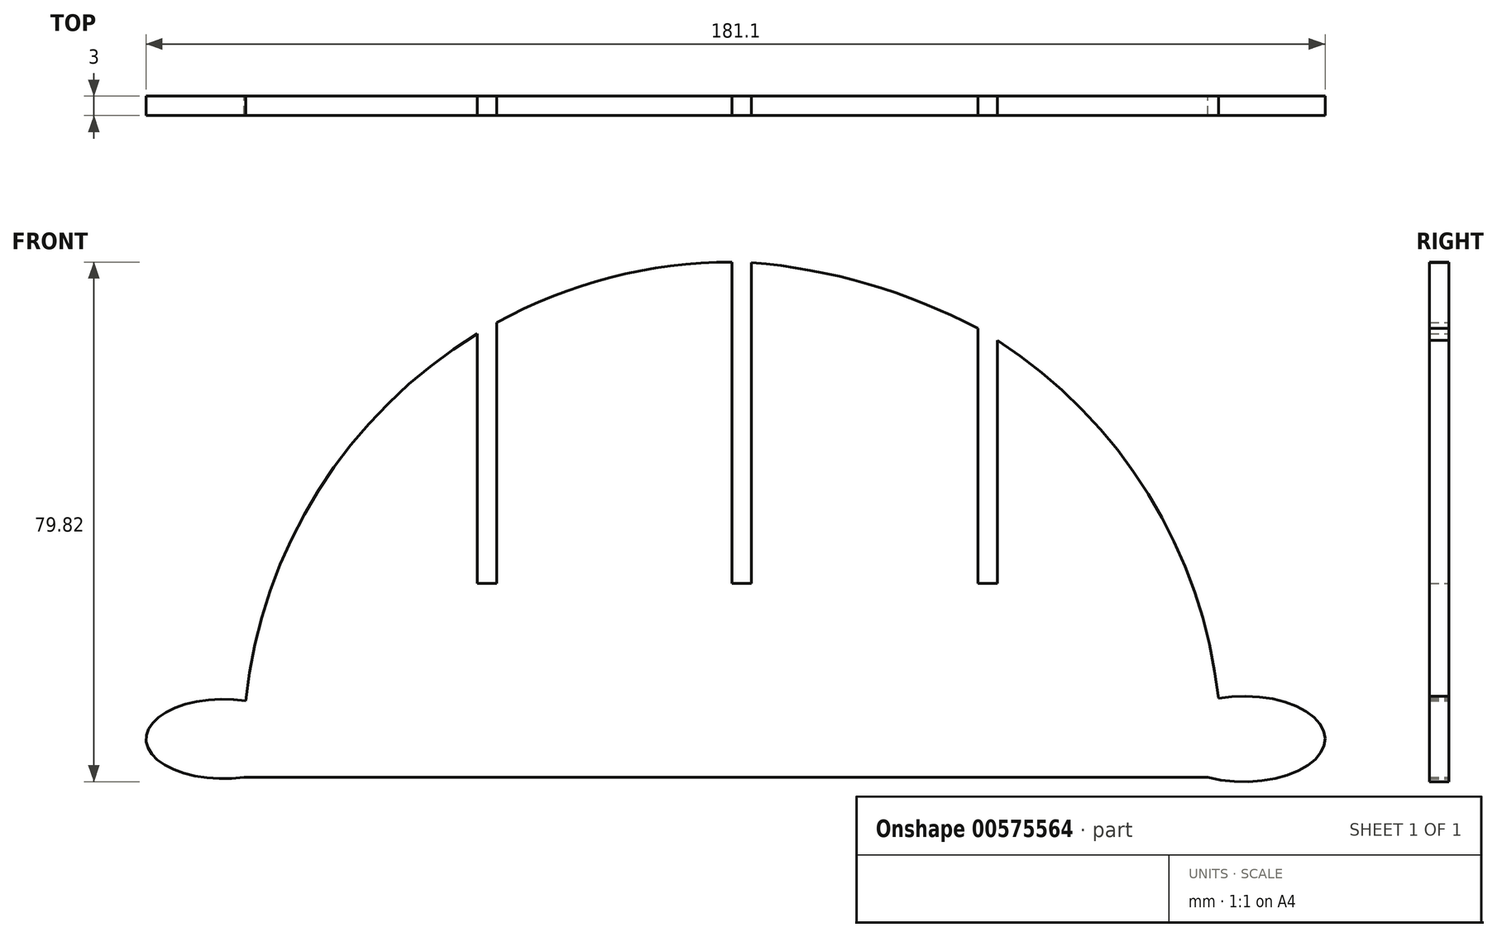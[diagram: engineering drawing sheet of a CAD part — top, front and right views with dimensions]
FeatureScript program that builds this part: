
annotation { "Feature Type Name" : "Feature", "Feature Type Description" : "" }
export const myFeature = defineFeature(function(context is Context, id is Id, definition is map)
    precondition{}
    {
        {
            var Q0;
            Q0=qCreatedBy(makeId("Front.planeOp"),FACE);
            var sketch = newSketch(context, id + "F0", { "sketchPlane" : qUnion([Q0])});
            skLineSegment(sketch, "E0", {"start": v(70.95, 0) * mm, "end": v(-79.05, 0) * mm});
            skArc(sketch, "E1.trimOffspring", {"start": v(70.65, 11.7) * mm, "mid": v(70.63, 11.92) * mm, "end": v(70.6, 12.13) * mm});
            skLineSegment(sketch, "E2", {"start": v(36.67, 29.76) * mm, "end": v(33.67, 29.76) * mm});
            skPoint(sketch, "E3.end.orphan", {"position": v(43.59, 29.76) * mm});
            skPoint(sketch, "E4.start.orphan", {"position": v(33.67, 68.95) * mm});
            skLineSegment(sketch, "E5", {"start": v(-1.1, 29.76) * mm, "end": v(-4.1, 29.76) * mm});
            skLineSegment(sketch, "E6", {"start": v(-40.23, 29.76) * mm, "end": v(-43.23, 29.76) * mm});
            skPoint(sketch, "E7.orphan", {"position": v(66.5, 29.76) * mm});
            skEllipticalArc(sketch, "E8", {});
            skPoint(sketch, "E9.orphan", {"position": v(-80.82, 0) * mm});
            skEllipticalArc(sketch, "E10", {});
            skArc(sketch, "E11.trimOffspring", {"start": v(70.62, 12.14) * mm, "mid": v(59.87, 43.47) * mm, "end": v(36.67, 67.14) * mm});
            skLineSegment(sketch, "E12", {"start": v(-40.23, 29.76) * mm, "end": v(-40.23, 69.85) * mm});
            skLineSegment(sketch, "E13", {"start": v(-43.23, 29.76) * mm, "end": v(-43.23, 68.11) * mm});
            skArc(sketch, "E14.trimOffspring", {"start": v(-43.23, 68.11) * mm, "mid": v(-67.63, 44.04) * mm, "end": v(-78.8, 11.63) * mm});
            skLineSegment(sketch, "E15", {"start": v(-1.1, 29.76) * mm, "end": v(-1.1, 79.08) * mm});
            skLineSegment(sketch, "E16", {"start": v(-4.1, 29.76) * mm, "end": v(-4.1, 79.14) * mm});
            skArc(sketch, "E17.trimOffspring", {"start": v(-4.1, 79.14) * mm, "mid": v(-22.75, 76.77) * mm, "end": v(-40.23, 69.85) * mm});
            skLineSegment(sketch, "E18", {"start": v(36.67, 29.76) * mm, "end": v(36.67, 67.14) * mm});
            skLineSegment(sketch, "E19", {"start": v(33.67, 68.95) * mm, "end": v(33.67, 29.76) * mm});
            skArc(sketch, "E20", {"start": v(33.67, 68.95) * mm, "mid": v(16.8, 75.78) * mm, "end": v(-1.1, 79.08) * mm});
            const initialGuessF0  = {"E8": [0.0745469480752945, 0.005894604604691267, 1, 0, 0.012467116117477417, 0.006575280191314619, 4.253351988137473, 1.8927247065415773], "E10": [-0.08218461689231028, 0.0058946046046912315, 1, 0, 0.011900432407855988, 0.006111084969047646, 1.2750591683167358, 4.979354728818344]};
            skSetInitialGuess(sketch, initialGuessF0);
            skSolve(sketch);
        }
        {
            var Q0;
            Q0=qSketchRegion(id+"F0",true);
            extrude(context, id + "F1", {"entities" : qUnion([Q0]), "depth" : 3 * mm, "offsetDistance" : 25 * mm});
        }
    });
